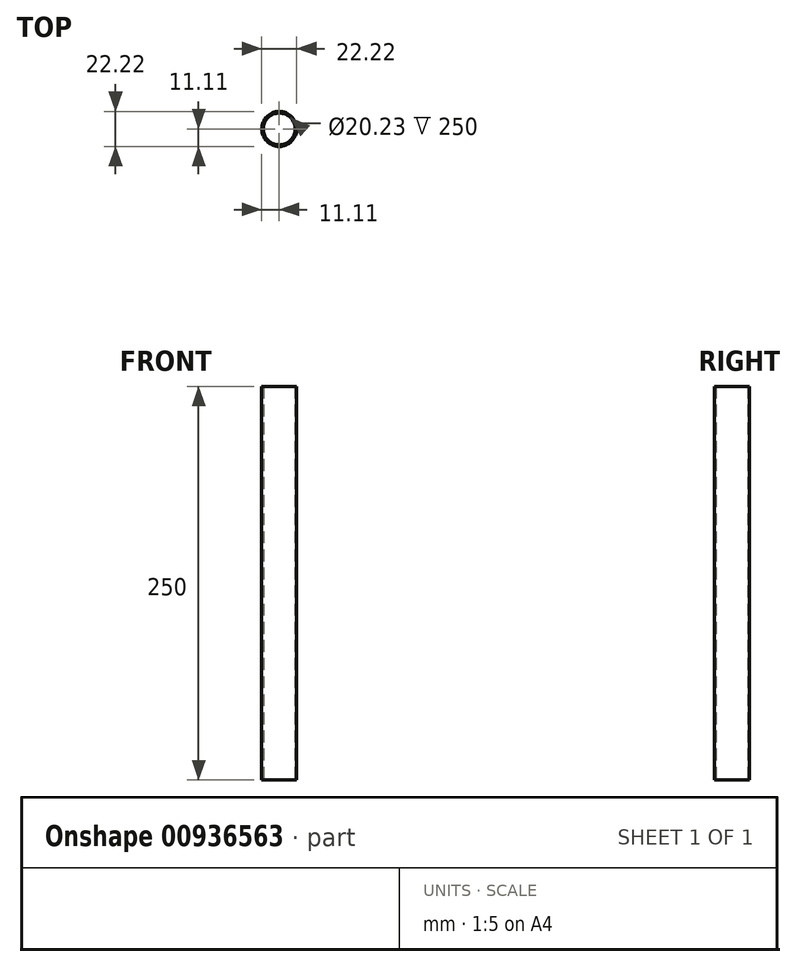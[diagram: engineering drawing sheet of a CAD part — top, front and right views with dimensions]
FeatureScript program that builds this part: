
annotation { "Feature Type Name" : "Feature", "Feature Type Description" : "" }
export const myFeature = defineFeature(function(context is Context, id is Id, definition is map)
    precondition{}
    {
        {
            var Q0;
            Q0=qCreatedBy(makeId("Top.planeOp"),FACE);
            var sketch = newSketch(context, id + "F0", { "sketchPlane" : qUnion([Q0])});
            skCircle(sketch, "E0", {"center": v(0, 0) * mm, "radius": 11.11 * mm});
            skCircle(sketch, "E1", {"center": v(0, 0) * mm, "radius": 10.11 * mm});
            skSolve(sketch);
        }
        {
            var Q0;
            Q0 = qSketchRegion(id + "F0", true);
            extrude(context, id + "F1", {"entities" : qUnion([Q0]), "depth" : 250 * mm, "offsetDistance" : 25 * mm});
        }
    });
